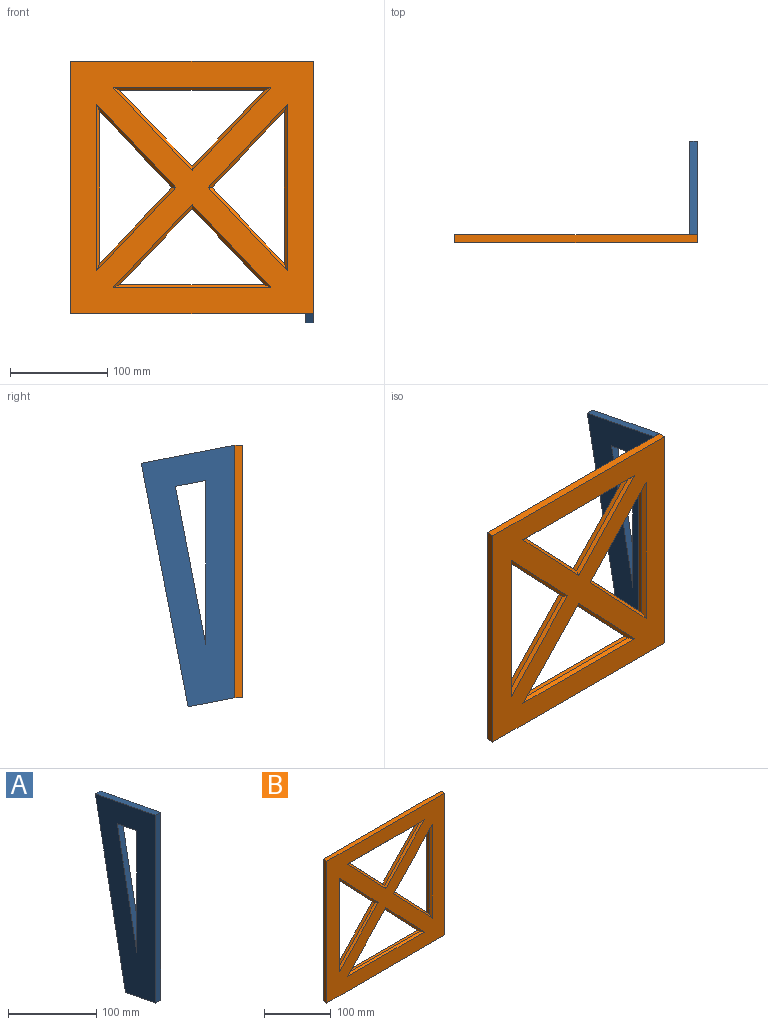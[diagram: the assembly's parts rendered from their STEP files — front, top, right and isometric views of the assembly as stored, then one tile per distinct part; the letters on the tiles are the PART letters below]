
ASSEMBLY  parts=2 mates=1
PART A: 9 faces, bbox 8x96.4x269.3 mm
  f0: plane 31.31x8mm, normal (0,-0.19,-0.98), area 255.1mm2, adj f1,f6,f7,f8
  f1: plane 162.8x31.31mm, normal (0,-0.98,0.19), area 1326.3mm2, adj f0,f6,f7,f8
  f2: plane 96.43x18.55mm, normal (0,0.19,0.98), area 785.6mm2, adj f3,f5,f7,f8
  f3: plane 260x8mm, normal (0,-1,0), area 2080mm2, adj f2,f4,f7,f8
  f4: plane 48.22x9.27mm, normal (0,-0.19,-0.98), area 392.8mm2, adj f3,f5,f7,f8
  f5: plane 250.73x48.22mm, normal (0,0.98,-0.19), area 2042.6mm2, adj f2,f4,f7,f8
  f6: plane 168.82x8mm, normal (0,1,0), area 1350.6mm2, adj f0,f1,f7,f8
  f7: plane 269.27x96.43mm, normal (1,0,0), area 16161.8mm2, adj f0,f1,f2,f3,f4,f5,f6
  f8: plane 269.27x96.43mm, normal (-1,0,0), area 16161.8mm2, adj f0,f1,f2,f3,f4,f5,f6
PART B: 30 faces, bbox 250x8x260 mm
  f0: plane 260x250mm, normal (0,-1,0), area 37119.5mm2, adj f2,f3,f4,f5,f18,f19,f20,f21
  f1: plane 260x250mm, normal (0,1,0), area 41749.4mm2, adj f2,f3,f4,f5,f6,f7,f8,f9
  f2: plane 260x8mm, normal (-1,0,0), area 2080mm2, adj f0,f1,f3,f5
  f3: plane 250x8mm, normal (0,0,-1), area 2000mm2, adj f0,f1,f2,f4
  f4: plane 260x8mm, normal (1,0,0), area 2080mm2, adj f0,f1,f3,f5
  f5: plane 250x8mm, normal (0,0,1), area 2000mm2, adj f0,f1,f2,f4
  f6: plane 148.62x5mm, normal (0,0,-1), area 743.1mm2, adj f1,f7,f8,f20
  f7: plane 78.22x74.31mm, normal (0.72,0,0.69), area 539.5mm2, adj f1,f6,f8,f18
  f8: plane 78.22x74.31mm, normal (-0.72,0,0.69), area 539.5mm2, adj f1,f6,f7,f19
  f9: plane 78.22x74.31mm, normal (0.72,0,0.69), area 539.5mm2, adj f1,f10,f11,f22
  f10: plane 156.44x5mm, normal (-1,0,0), area 782.2mm2, adj f1,f9,f11,f21
  f11: plane 78.22x74.31mm, normal (0.72,0,-0.69), area 539.5mm2, adj f1,f9,f10,f23
  f12: plane 156.44x5mm, normal (1,0,0), area 782.2mm2, adj f1,f13,f14,f28
  f13: plane 78.22x74.31mm, normal (-0.72,0,0.69), area 539.5mm2, adj f1,f12,f14,f29
  f14: plane 78.22x74.31mm, normal (-0.72,0,-0.69), area 539.5mm2, adj f1,f12,f13,f27
  f15: plane 78.22x74.31mm, normal (0.72,0,-0.69), area 539.5mm2, adj f1,f16,f17,f24
  f16: plane 148.62x5mm, normal (0,0,1), area 743.1mm2, adj f1,f15,f17,f25
  f17: plane 78.22x74.31mm, normal (-0.72,0,-0.69), area 539.5mm2, adj f1,f15,f16,f26
  f18: plane 85.58x81.3mm, normal (0.51,-0.71,0.49), area 479.3mm2, adj f0,f7,f19,f20
  f19: plane 85.58x81.3mm, normal (-0.51,-0.71,0.49), area 479.3mm2, adj f0,f8,f18,f20
  f20: plane 162.6x3mm, normal (0,-0.71,-0.71), area 660.2mm2, adj f0,f6,f18,f19
  f21: plane 171.47x3mm, normal (-0.71,-0.71,0), area 695.6mm2, adj f0,f10,f22,f23
  f22: plane 85.74x81.45mm, normal (0.51,-0.71,0.49), area 479.7mm2, adj f0,f9,f21,f23
  f23: plane 85.74x81.45mm, normal (0.51,-0.71,-0.49), area 479.7mm2, adj f0,f11,f21,f22
  f24: plane 85.58x81.3mm, normal (0.51,-0.71,-0.49), area 479.3mm2, adj f0,f15,f25,f26
  f25: plane 162.6x3mm, normal (0,-0.71,0.71), area 660.2mm2, adj f0,f16,f24,f26
  f26: plane 85.58x81.3mm, normal (-0.51,-0.71,-0.49), area 479.3mm2, adj f0,f17,f24,f25
  f27: plane 85.74x81.45mm, normal (-0.51,-0.71,-0.49), area 479.7mm2, adj f0,f14,f28,f29
  f28: plane 171.47x3mm, normal (0.71,-0.71,0), area 695.6mm2, adj f0,f12,f27,f29
  f29: plane 85.74x81.45mm, normal (-0.51,-0.71,0.49), area 479.7mm2, adj f0,f13,f27,f28
PLACE A t=(181.47,101.56,-61.33)mm
PLACE B t=(-60.53,101.56,-61.33)mm
MATE fastened B.f1 <-> A.f3  axis (0,1,0) through (189.47,101.56,198.67)mm
